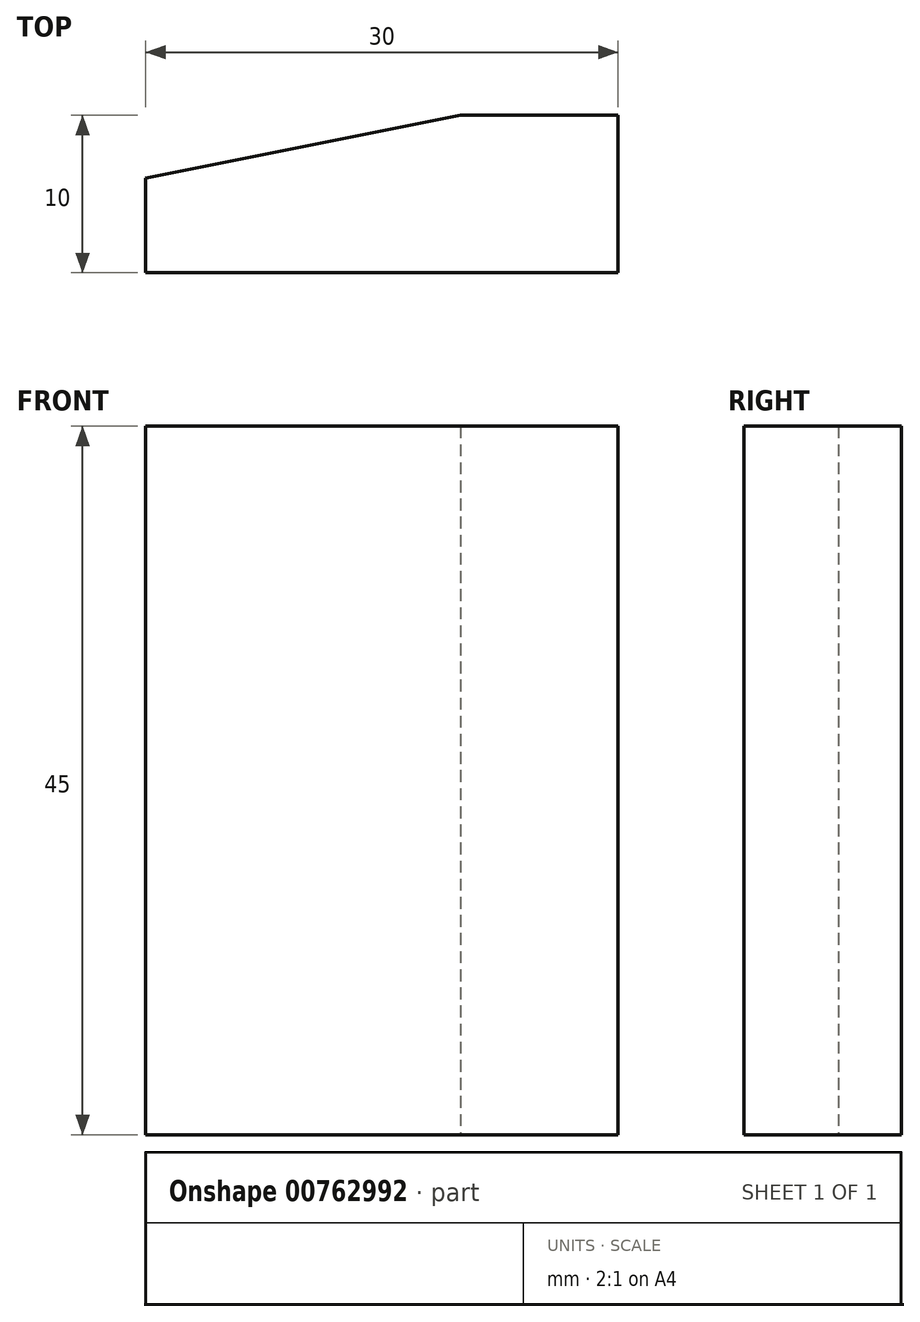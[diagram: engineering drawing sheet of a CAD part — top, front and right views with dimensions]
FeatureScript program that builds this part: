
annotation { "Feature Type Name" : "Feature", "Feature Type Description" : "" }
export const myFeature = defineFeature(function(context is Context, id is Id, definition is map)
    precondition{}
    {
        {
            var Q0;
            Q0=qCreatedBy(makeId("Top.planeOp"),FACE);
            var sketch = newSketch(context, id + "F0", { "sketchPlane" : qUnion([Q0])});
            skLineSegment(sketch, "E0", {"start": v(-15, 1) * mm, "end": v(5, 5) * mm});
            skLineSegment(sketch, "E1", {"start": v(-15, 1) * mm, "end": v(-15, -5) * mm});
            skLineSegment(sketch, "E2", {"start": v(-15, -5) * mm, "end": v(15, -5) * mm});
            skLineSegment(sketch, "E3", {"start": v(15, -5) * mm, "end": v(15, 5) * mm});
            skLineSegment(sketch, "E4", {"start": v(15, 5) * mm, "end": v(5, 5) * mm});
            skSolve(sketch);
        }
        {
            var Q0;
            Q0=makeQuery(id+"F0.imprint","IMPRINT",FACE,{"disambiguationData":[TD([[makeQuery(id+"F0.imprint","IMPRINT",EDGE,{"derivedFrom":sQuery(id+"F0.wireOp",EDGE,"E0")}),-1.0]])]});
            extrude(context, id + "F1", {"entities" : qUnion([Q0]), "depth" : 45 * mm, "offsetDistance" : 25 * mm});
        }
    });
